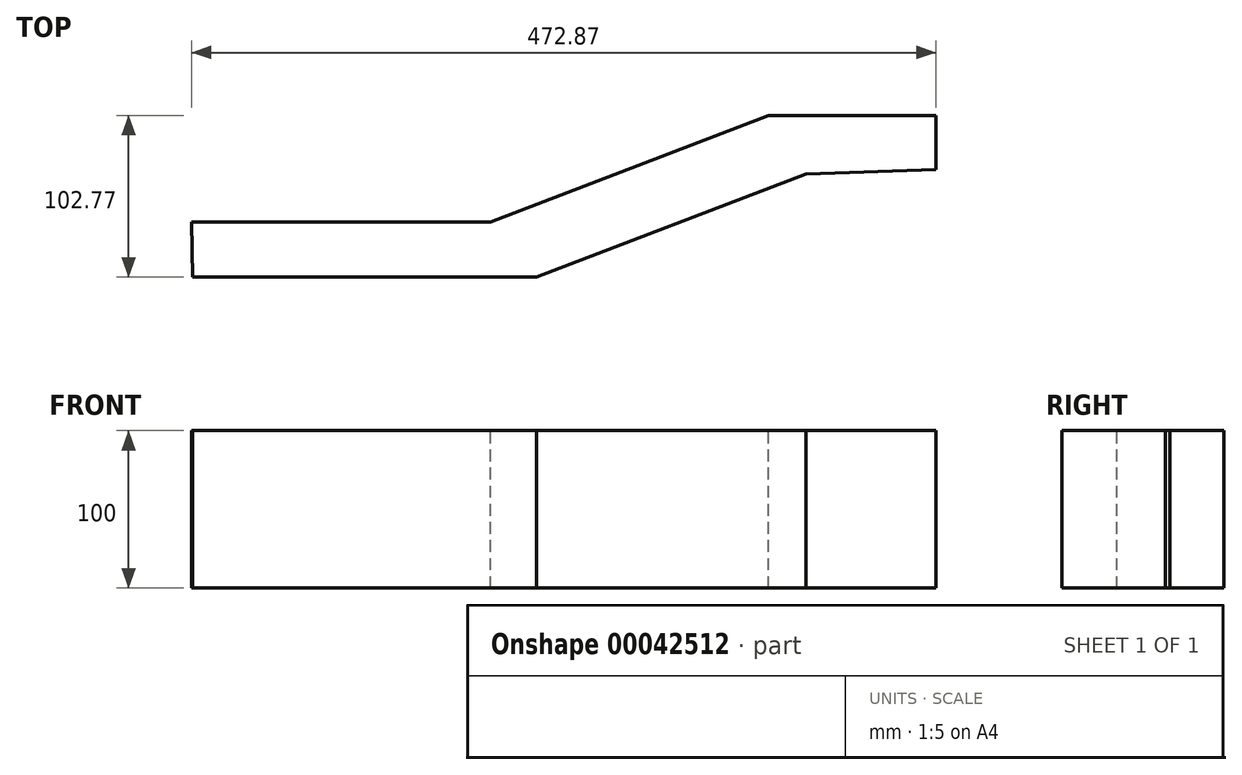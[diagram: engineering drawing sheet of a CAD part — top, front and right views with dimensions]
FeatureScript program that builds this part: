
annotation { "Feature Type Name" : "Feature", "Feature Type Description" : "" }
export const myFeature = defineFeature(function(context is Context, id is Id, definition is map)
    precondition{}
    {
        {
            var Q0;
            Q0=qCreatedBy(makeId("Top.planeOp"),FACE);
            var sketch = newSketch(context, id + "F0", { "sketchPlane" : qUnion([Q0])});
            skLineSegment(sketch, "E0", {"start": v(-257.42, 12.08) * mm, "end": v(-67.53, 12.08) * mm});
            skLineSegment(sketch, "E1", {"start": v(-67.53, 12.08) * mm, "end": v(108.96, 79.85) * mm});
            skLineSegment(sketch, "E2", {"start": v(108.96, 79.85) * mm, "end": v(132.79, 42.61) * mm});
            skLineSegment(sketch, "E3", {"start": v(132.79, 42.61) * mm, "end": v(-38.49, -22.92) * mm});
            skLineSegment(sketch, "E4", {"start": v(-38.49, -22.92) * mm, "end": v(-256.68, -22.92) * mm});
            skLineSegment(sketch, "E5", {"start": v(-256.68, -22.92) * mm, "end": v(-257.42, 12.08) * mm});
            skLineSegment(sketch, "E6", {"start": v(108.96, 79.85) * mm, "end": v(215.45, 79.85) * mm});
            skLineSegment(sketch, "E7", {"start": v(215.45, 79.85) * mm, "end": v(215.45, 45.6) * mm});
            skLineSegment(sketch, "E8", {"start": v(215.45, 45.6) * mm, "end": v(132.79, 42.61) * mm});
            skSolve(sketch);
        }
        {
            var Q0;
            Q0=makeQuery(id+"F0.imprint","IMPRINT",FACE,{"disambiguationData":[TD([[makeQuery(id+"F0.imprint","IMPRINT",EDGE,{"derivedFrom":sQuery(id+"F0.wireOp",EDGE,"E0")}),-1.0]])]});
            var Q1;
            Q1=makeQuery(id+"F0.imprint","IMPRINT",FACE,{"disambiguationData":[TD([[makeQuery(id+"F0.imprint","IMPRINT",EDGE,{"derivedFrom":sQuery(id+"F0.wireOp",EDGE,"E2")}),1.0]])]});
            extrude(context, id + "F1", {"entities" : qUnion([Q0, Q1]), "oppositeDirection" : true, "depth" : 100 * mm});
        }
    });
